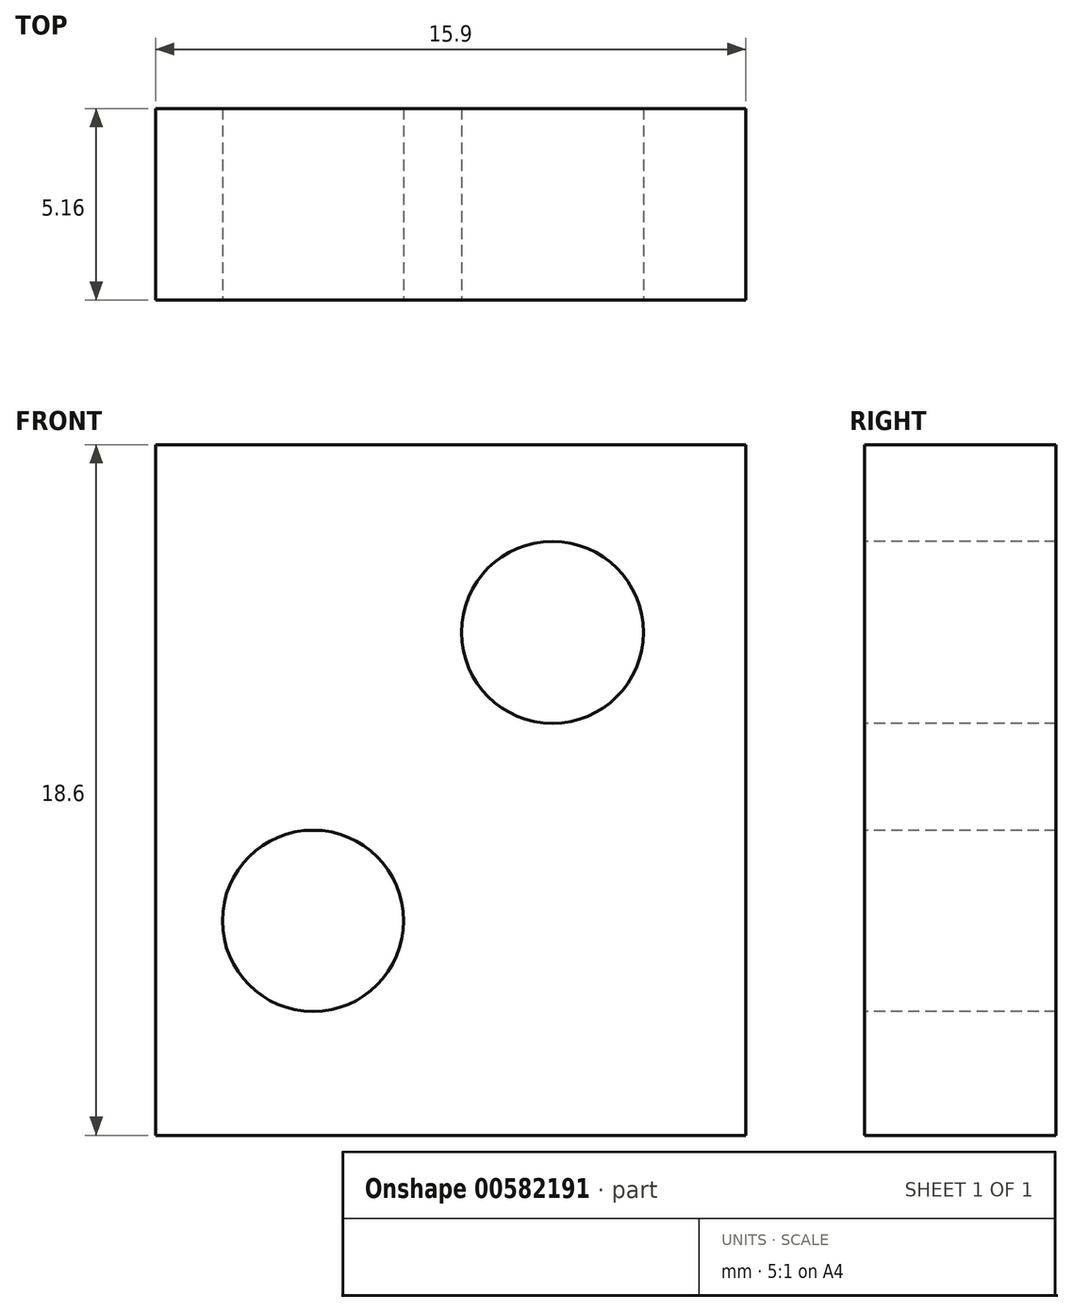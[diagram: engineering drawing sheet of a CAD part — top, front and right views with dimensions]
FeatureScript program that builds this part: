
annotation { "Feature Type Name" : "Feature", "Feature Type Description" : "" }
export const myFeature = defineFeature(function(context is Context, id is Id, definition is map)
    precondition{}
    {
        {
            var Q0;
            Q0=qCreatedBy(makeId("Front.planeOp"),FACE);
            var sketch = newSketch(context, id + "F0", { "sketchPlane" : qUnion([Q0])});
            skLineSegment(sketch, "E0.bottom", {"start": v(-9.55, 0.22) * mm, "end": v(6.35, 0.22) * mm});
            skLineSegment(sketch, "E0.top", {"start": v(-9.55, -18.38) * mm, "end": v(6.35, -18.38) * mm});
            skLineSegment(sketch, "E0.left", {"start": v(-9.55, 0.22) * mm, "end": v(-9.55, -18.38) * mm});
            skLineSegment(sketch, "E0.right", {"start": v(6.35, 0.22) * mm, "end": v(6.35, -18.38) * mm});
            skSolve(sketch);
        }
        {
            var Q0;
            Q0=makeQuery(id+"F0.imprint","IMPRINT",FACE,{"disambiguationData":[TD([[makeQuery(id+"F0.imprint","IMPRINT",EDGE,{"derivedFrom":sQuery(id+"F0.wireOp",EDGE,"E0.bottom")}),-1.0]])]});
            extrude(context, id + "F1", {"entities" : qUnion([Q0]), "depth" : 5.16 * mm, "offsetDistance" : 25 * mm});
        }
        {
            var Q0;
            Q0=makeQuery(id+"F1.opExtrude","CAP_FACE",FACE,{"disambiguationData":[OSD([sQuery(id+"F0.wireOp",EDGE,"E0.bottom"),sQuery(id+"F0.wireOp",EDGE,"E0.top"),sQuery(id+"F0.wireOp",EDGE,"E0.left"),sQuery(id+"F0.wireOp",EDGE,"E0.right")])],"isStart":false});
            var sketch = newSketch(context, id + "F2", { "sketchPlane" : qUnion([Q0])});
            skCircle(sketch, "E1", {"center": v(1.14, -4.83) * mm, "radius": 2.45 * mm});
            skSolve(sketch);
        }
        {
            var Q0;
            Q0=makeQuery(id+"F2.imprint","IMPRINT",FACE,{"disambiguationData":[TD([[makeQuery(id+"F2.imprint","IMPRINT",EDGE,{"derivedFrom":sQuery(id+"F2.wireOp",EDGE,"E1")}),1.0]])]});
            extrude(context, id + "F3", {"entities" : qUnion([Q0]), "operationType" : NewBodyOperationType.REMOVE, "endBound" : BoundingType.THROUGH_ALL, "oppositeDirection" : true, "depth" : 25 * mm, "offsetDistance" : 25 * mm});
        }
        {
            var Q0;
            Q0=makeQuery(id+"F1.opExtrude","CAP_FACE",FACE,{"disambiguationData":[OSD([sQuery(id+"F0.wireOp",EDGE,"E0.bottom"),sQuery(id+"F0.wireOp",EDGE,"E0.top"),sQuery(id+"F0.wireOp",EDGE,"E0.left"),sQuery(id+"F0.wireOp",EDGE,"E0.right")])],"isStart":false});
            var sketch = newSketch(context, id + "F4", { "sketchPlane" : qUnion([Q0])});
            skCircle(sketch, "E2", {"center": v(-5.3, -12.6) * mm, "radius": 2.44 * mm});
            skSolve(sketch);
        }
        {
            var Q0;
            Q0=makeQuery(id+"F4.imprint","IMPRINT",FACE,{"disambiguationData":[TD([[makeQuery(id+"F4.imprint","IMPRINT",EDGE,{"derivedFrom":sQuery(id+"F4.wireOp",EDGE,"E2")}),1.0]])]});
            extrude(context, id + "F5", {"entities" : qUnion([Q0]), "operationType" : NewBodyOperationType.REMOVE, "endBound" : BoundingType.THROUGH_ALL, "oppositeDirection" : true, "depth" : 25 * mm, "offsetDistance" : 25 * mm});
        }
    });
